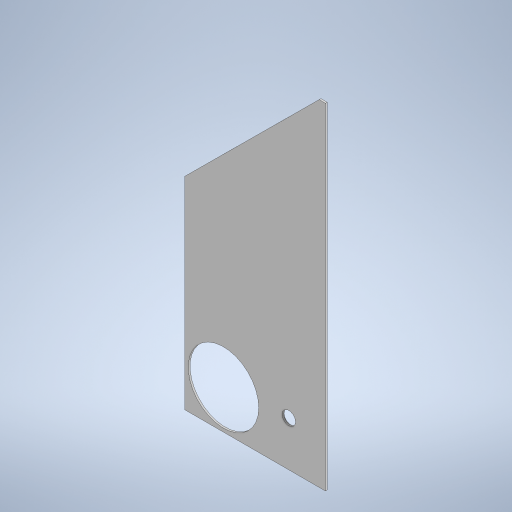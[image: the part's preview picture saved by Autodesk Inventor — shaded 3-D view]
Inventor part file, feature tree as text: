
AUTODESK INVENTOR PART (.ipt)
format: ipt  version: 2024.2 (Build 282272000, 272)  size: 319,488 bytes
history: native  units: mm
features: extrude x3, sketch x2, projected_geometry x1, other x1
ambient origin geometry x8: Origin, YZ Plane, XZ Plane, XY Plane, X Axis, Y Axis, Z Axis, Center Point
bodies: Solid1 (feature_tree)
feature tree (7):
  extrude  "Extrusion1"  Depth=1150.0mm
  extrude  "Extrusion3"  Depth=1180.0mm
  extrude  "Extrusion4"  Depth=10.0mm
  sketch  "Sketch3"  dims[d1=840.0mm d3=1150.0mm]
  sketch  "Sketch4"  dims[d11=390.0mm d12=1180.0mm d13=950.0mm d14=76.0mm d15=1910.0mm d16=255.0mm d17=220.0mm d18=401.0mm d19=220.0mm d21=1277.0mm d22=1554.635823mm d23=100.0mm d24=10.0mm d25=0.0mm d33=2140.0mm d34=494.0mm d37=10.0mm d38=0.0mm d45=310.0mm d47=5.0mm d48=80.0mm d49=372.0mm d51=780.0mm d52=1078.0mm d53=1340.0mm d54=0.0mm d55=0.0mm]
  projected_geometry  "Projected Loop1"
  other  "Definition1"
